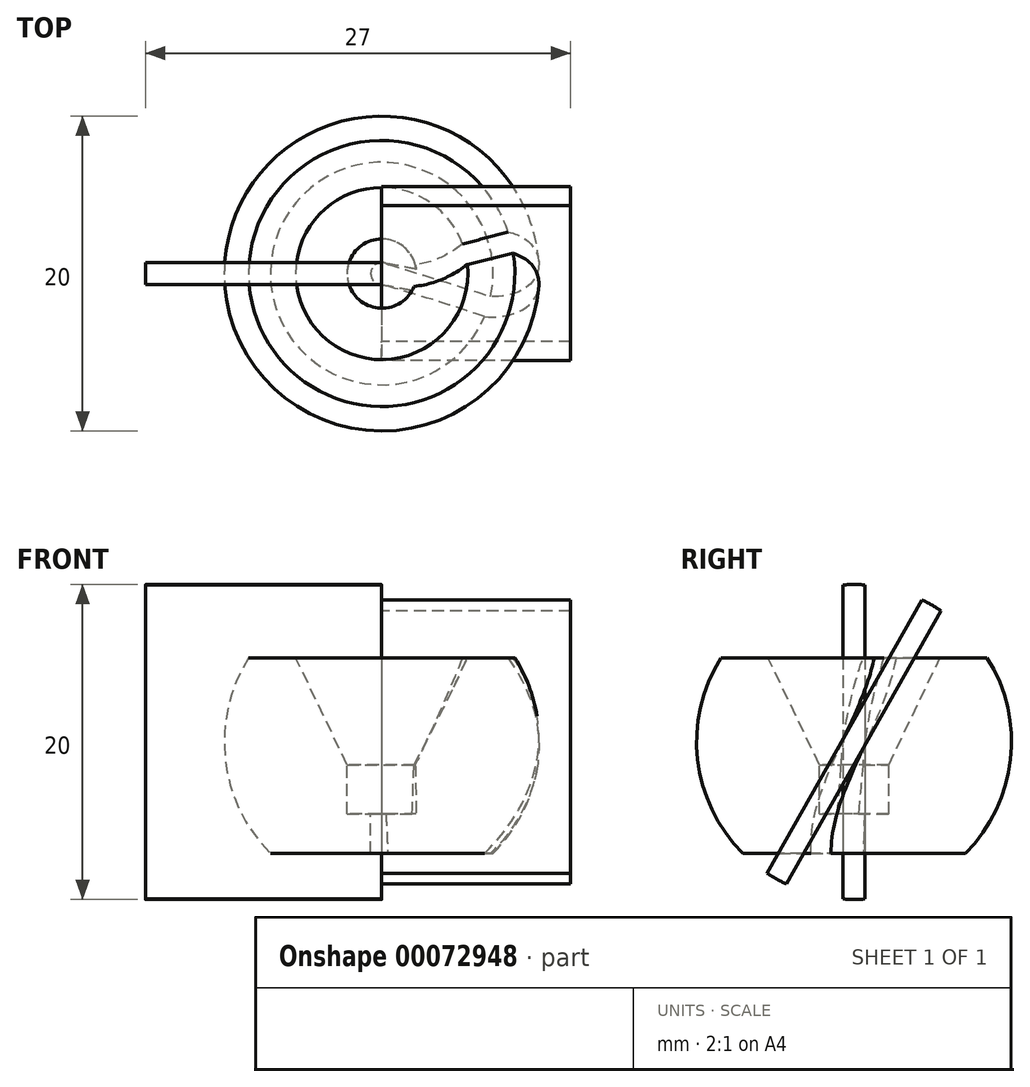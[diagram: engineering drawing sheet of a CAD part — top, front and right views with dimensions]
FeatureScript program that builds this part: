
annotation { "Feature Type Name" : "Feature", "Feature Type Description" : "" }
export const myFeature = defineFeature(function(context is Context, id is Id, definition is map)
    precondition{}
    {
        {
            var Q0;
            Q0=qCreatedBy(makeId("Front.planeOp"),FACE);
            var sketch = newSketch(context, id + "F0", { "sketchPlane" : qUnion([Q0])});
            skCircle(sketch, "E0", {"center": v(0, 43.52) * mm, "radius": 10 * mm});
            skLineSegment(sketch, "E1", {"start": v(-8.45, 48.86) * mm, "end": v(8.45, 48.86) * mm});
            skLineSegment(sketch, "E2", {"start": v(0.7, 33.54) * mm, "end": v(0.7, 38.95) * mm});
            skLineSegment(sketch, "E3", {"start": v(0.7, 38.95) * mm, "end": v(5.46, 48.86) * mm});
            skLineSegment(sketch, "E4", {"start": v(0, 48.86) * mm, "end": v(0, 33.52) * mm});
            skLineSegment(sketch, "E5", {"start": v(7.07, 36.45) * mm, "end": v(0, 29.38) * mm});
            skLineSegment(sketch, "E6", {"start": v(7.07, 36.45) * mm, "end": v(0, 36.45) * mm});
            skLineSegment(sketch, "E7", {"start": v(0, 53.52) * mm, "end": v(0, 48.86) * mm});
            skLineSegment(sketch, "E8", {"start": v(0.7, 38.95) * mm, "end": v(2.2, 38.95) * mm});
            skLineSegment(sketch, "E9", {"start": v(2.2, 38.95) * mm, "end": v(2.2, 42.07) * mm});
            skSolve(sketch);
        }
        {
            var Q0;
            {var subQ8=sQuery(id+"F0.wireOp",EDGE,"E8");Q0=makeQuery(id+"F0.imprint","IMPRINT",FACE,{"disambiguationData":[TD([[makeQuery(id+"F0.imprint","IMPRINT",EDGE,{"derivedFrom":subQ8}),-1.0]])]});}
            var Q1;
            Q1=sQuery(id+"F0.wireOp",EDGE,"E4");
            revolve(context, id + "F1", {"entities" : qUnion([Q0]), "axis" : qUnion([Q1]), "revolveType" : RevolveType.FULL});
        }
        {
            var Q0;
            Q0=qCreatedBy(makeId("Right.planeOp"),FACE);
            var sketch = newSketch(context, id + "F2", { "sketchPlane" : qUnion([Q0])});
            skCircle(sketch, "E10", {"center": v(0, 43.52) * mm, "radius": 10 * mm});
            skLineSegment(sketch, "E11.0", {"start": v(0, 53.52) * mm, "end": v(0, 48.86) * mm});
            skLineSegment(sketch, "E12.0", {"start": v(0, 48.86) * mm, "end": v(0, 33.52) * mm, "construction": true});
            skLineSegment(sketch, "E13", {"start": v(4.93, 52.22) * mm, "end": v(-4.93, 34.82) * mm, "construction": true});
            skLineSegment(sketch, "E14", {"start": v(5.52, 51.85) * mm, "end": v(-4.3, 34.5) * mm});
            skLineSegment(sketch, "E15", {"start": v(4.3, 52.54) * mm, "end": v(-5.52, 35.18) * mm});
            skLineSegment(sketch, "E16", {"start": v(-0.7, 53.5) * mm, "end": v(-0.7, 33.54) * mm});
            skLineSegment(sketch, "E17", {"start": v(0.7, 53.5) * mm, "end": v(0.7, 33.54) * mm});
            skSolve(sketch);
        }
        {
            var Q0;
            {var subQ0=sQuery(id+"F2.wireOp",EDGE,"E14");var subQ1=sQuery(id+"F2.wireOp",EDGE,"E10");var subQ2=makeQuery(id+"F2.imprint","INTERSECT",VERTEX,{"disambiguationData":[OD(1.0)],"derivedFrom":[subQ1,subQ0]});Q0=makeQuery(id+"F2.imprint","IMPRINT",FACE,{"disambiguationData":[TD([[makeQuery(id+"F2.imprint","IMPRINT",EDGE,{"disambiguationData":[TD([[subQ2,1.0]])],"derivedFrom":subQ1}),1.0]])]});}
            var Q1;
            {var subQ0=sQuery(id+"F2.wireOp",EDGE,"E17");var subQ1=sQuery(id+"F2.wireOp",EDGE,"E14");var subQ2=makeQuery(id+"F2.imprint","INTERSECT",VERTEX,{"derivedFrom":[subQ1,subQ0]});Q1=makeQuery(id+"F2.imprint","IMPRINT",FACE,{"disambiguationData":[TD([[makeQuery(id+"F2.imprint","IMPRINT",EDGE,{"disambiguationData":[TD([[subQ2,-1.0]])],"derivedFrom":subQ1}),-1.0]])]});}
            var Q2;
            {var subQ0=sQuery(id+"F2.wireOp",EDGE,"E14");var subQ1=sQuery(id+"F2.wireOp",EDGE,"E10");var subQ2=makeQuery(id+"F2.imprint","INTERSECT",VERTEX,{"disambiguationData":[OD(0.0)],"derivedFrom":[subQ1,subQ0]});Q2=makeQuery(id+"F2.imprint","IMPRINT",FACE,{"disambiguationData":[TD([[makeQuery(id+"F2.imprint","IMPRINT",EDGE,{"disambiguationData":[TD([[subQ2,-1.0]])],"derivedFrom":subQ1}),1.0]])]});}
            extrude(context, id + "F3", {"entities" : qUnion([Q0, Q1, Q2]), "depth" : 12 * mm});
        }
        {
            var Q0;
            {var subQ1=sQuery(id+"F2.wireOp",EDGE,"E10");var subQ8=makeQuery(id+"F2.imprint","IMPRINT",VERTEX,{"derivedFrom":subQ1});Q0=makeQuery(id+"F2.imprint","IMPRINT",FACE,{"disambiguationData":[TD([[makeQuery(id+"F2.imprint","IMPRINT",EDGE,{"disambiguationData":[TD([[subQ8,1.0]])],"derivedFrom":subQ1}),1.0]])]});}
            var Q1;
            {var subQ0=sQuery(id+"F2.wireOp",EDGE,"E17");var subQ1=sQuery(id+"F2.wireOp",EDGE,"E14");var subQ2=makeQuery(id+"F2.imprint","INTERSECT",VERTEX,{"derivedFrom":[subQ1,subQ0]});Q1=makeQuery(id+"F2.imprint","IMPRINT",FACE,{"disambiguationData":[TD([[makeQuery(id+"F2.imprint","IMPRINT",EDGE,{"disambiguationData":[TD([[subQ2,-1.0]])],"derivedFrom":subQ1}),-1.0]])]});}
            var Q2;
            {var subQ0=sQuery(id+"F2.wireOp",EDGE,"E16");var subQ1=sQuery(id+"F2.wireOp",EDGE,"E10");var subQ2=makeQuery(id+"F2.imprint","INTERSECT",VERTEX,{"disambiguationData":[OD(1.0)],"derivedFrom":[subQ1,subQ0]});Q2=makeQuery(id+"F2.imprint","IMPRINT",FACE,{"disambiguationData":[TD([[makeQuery(id+"F2.imprint","IMPRINT",EDGE,{"disambiguationData":[TD([[subQ2,-1.0]])],"derivedFrom":subQ1}),1.0]])]});}
            extrude(context, id + "F4", {"entities" : qUnion([Q0, Q1, Q2]), "oppositeDirection" : true, "depth" : 15 * mm});
        }
        {
            var Q0;
            Q0=makeQuery(id+"F3.opExtrude","CAP_FACE",FACE,{"disambiguationData":[OSD([sQuery(id+"F2.wireOp",EDGE,"E10"),sQuery(id+"F2.wireOp",EDGE,"E14"),sQuery(id+"F2.wireOp",EDGE,"E15")])],"isStart":false});
            var Q1;
            Q1=makeQuery(id+"F4.opExtrude","CAP_FACE",FACE,{"disambiguationData":[OSD([sQuery(id+"F2.wireOp",EDGE,"E10"),sQuery(id+"F2.wireOp",EDGE,"E16"),sQuery(id+"F2.wireOp",EDGE,"E17")])],"isStart":true});
            loft(context, id + "F5", {"sheetProfilesArray" : [{ "sheetProfileEntities" : qUnion([Q0]) }, { "sheetProfileEntities" : qUnion([Q1]) }]});
        }
        {
            var Q0;
            Q0=makeQuery(id+"F5.opLoft","SWEPT_BODY",BODY,{"disambiguationData":[OSD([sQuery(id+"F2.wireOp",EDGE,"E10"),sQuery(id+"F2.wireOp",EDGE,"E14"),sQuery(id+"F2.wireOp",EDGE,"E15"),sQuery(id+"F2.wireOp",EDGE,"E16"),sQuery(id+"F2.wireOp",EDGE,"E17")])]});
            var Q1;
            Q1=makeQuery(id+"F1.opRevolve","SWEPT_BODY",BODY,{"disambiguationData":[OSD([sQuery(id+"F0.wireOp",EDGE,"E0"),sQuery(id+"F0.wireOp",EDGE,"E1"),sQuery(id+"F0.wireOp",EDGE,"E2"),sQuery(id+"F0.wireOp",EDGE,"E3"),sQuery(id+"F0.wireOp",EDGE,"E6")])]});
            booleanBodies(context, id + "F6", {"operationType" : BooleanOperationType.SUBTRACTION, "tools" : qUnion([Q0]), "targets" : qUnion([Q1])});
        }
    });
